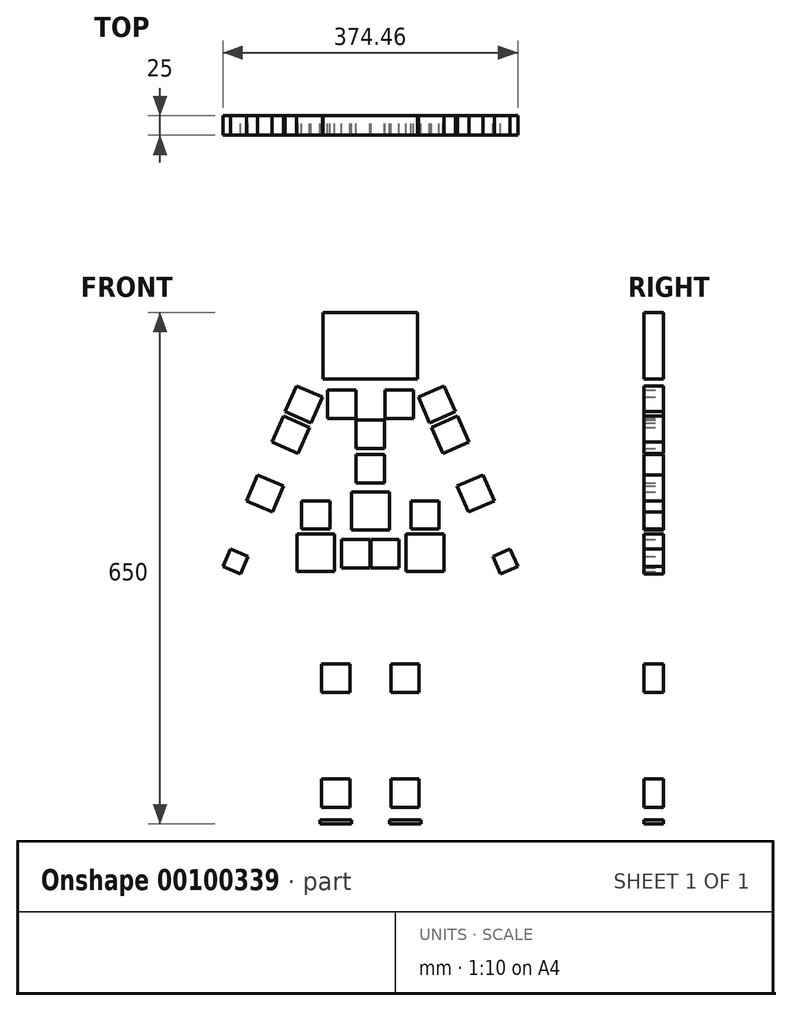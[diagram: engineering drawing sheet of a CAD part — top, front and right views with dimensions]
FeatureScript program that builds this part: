
annotation { "Feature Type Name" : "Feature", "Feature Type Description" : "" }
export const myFeature = defineFeature(function(context is Context, id is Id, definition is map)
    precondition{}
    {
        {
            var Q0;
            Q0=qCreatedBy(makeId("Front.planeOp"),FACE);
            var sketch = newSketch(context, id + "F0", { "sketchPlane" : qUnion([Q0])});
            skLineSegment(sketch, "E0.bottom", {"start": v(-190.27, 650) * mm, "end": v(190.27, 650) * mm, "construction": true});
            skLineSegment(sketch, "E0.top", {"start": v(-190.27, 0) * mm, "end": v(190.27, 0) * mm, "construction": true});
            skLineSegment(sketch, "E0.left", {"start": v(-190.27, 650) * mm, "end": v(-190.27, 0) * mm, "construction": true});
            skLineSegment(sketch, "E0.right", {"start": v(190.27, 650) * mm, "end": v(190.27, 0) * mm, "construction": true});
            skLineSegment(sketch, "E1", {"start": v(-190.27, 344.5) * mm, "end": v(190.27, 344.5) * mm, "construction": true});
            skLineSegment(sketch, "E2", {"start": v(-190.27, 234) * mm, "end": v(190.27, 234) * mm, "construction": true});
            skLineSegment(sketch, "E3", {"start": v(-190.27, 409.5) * mm, "end": v(190.27, 409.5) * mm, "construction": true});
            skLineSegment(sketch, "E4", {"start": v(-84.5, 650) * mm, "end": v(-84.5, 344.5) * mm, "construction": true});
            skLineSegment(sketch, "E5", {"start": v(84.5, 650) * mm, "end": v(84.5, 344.5) * mm, "construction": true});
            skLineSegment(sketch, "E6", {"start": v(0, 0) * mm, "end": v(0, 650) * mm, "construction": true});
            skLineSegment(sketch, "E7", {"start": v(-65, 344.5) * mm, "end": v(-65, 0) * mm, "construction": true});
            skLineSegment(sketch, "E8", {"start": v(65, 344.5) * mm, "end": v(65, 0) * mm, "construction": true});
            skLineSegment(sketch, "E9", {"start": v(-84.5, 565.5) * mm, "end": v(84.5, 565.5) * mm, "construction": true});
            skLineSegment(sketch, "E10", {"start": v(-190.27, 315.25) * mm, "end": v(190.27, 315.25) * mm, "construction": true});
            skLineSegment(sketch, "E11", {"start": v(-84.5, 471.25) * mm, "end": v(84.5, 471.25) * mm, "construction": true});
            skLineSegment(sketch, "E12", {"start": v(-65, 185.25) * mm, "end": v(65, 185.25) * mm, "construction": true});
            skLineSegment(sketch, "E13", {"start": v(-65, 39) * mm, "end": v(65, 39) * mm, "construction": true});
            skLineSegment(sketch, "E14", {"start": v(-84.5, 533) * mm, "end": v(84.5, 533) * mm, "construction": true});
            skSolve(sketch);
        }
        {
            var Q0;
            Q0=qCreatedBy(makeId("Front.planeOp"),FACE);
            var sketch = newSketch(context, id + "F1", { "sketchPlane" : qUnion([Q0])});
            skLineSegment(sketch, "E15", {"start": v(0, 344.5) * mm, "end": v(69.4, 344.5) * mm, "construction": true});
            skLineSegment(sketch, "E16", {"start": v(69.4, 344.5) * mm, "end": v(44, 185.25) * mm, "construction": true});
            skLineSegment(sketch, "E17", {"start": v(44, 185.25) * mm, "end": v(44, 39) * mm, "construction": true});
            skLineSegment(sketch, "E18", {"start": v(44, 39) * mm, "end": v(44, 0) * mm, "construction": true});
            skLineSegment(sketch, "E19", {"start": v(0, 0) * mm, "end": v(0, 650) * mm, "construction": true});
            skLineSegment(sketch, "E20.bottom", {"start": v(62, 21) * mm, "end": v(26, 21) * mm});
            skLineSegment(sketch, "E20.top", {"start": v(62, 57) * mm, "end": v(26, 57) * mm});
            skLineSegment(sketch, "E20.left", {"start": v(62, 21) * mm, "end": v(62, 57) * mm});
            skLineSegment(sketch, "E20.right", {"start": v(26, 21) * mm, "end": v(26, 57) * mm});
            skPoint(sketch, "E20.middle", {"position": v(44, 39) * mm});
            skLineSegment(sketch, "E21.bottom", {"start": v(62, 167.25) * mm, "end": v(26, 167.25) * mm});
            skLineSegment(sketch, "E21.top", {"start": v(62, 203.25) * mm, "end": v(26, 203.25) * mm});
            skLineSegment(sketch, "E21.left", {"start": v(62, 167.25) * mm, "end": v(62, 203.25) * mm});
            skLineSegment(sketch, "E21.right", {"start": v(26, 167.25) * mm, "end": v(26, 203.25) * mm});
            skPoint(sketch, "E21.middle", {"position": v(44, 185.25) * mm});
            skLineSegment(sketch, "E22.bottom", {"start": v(93.4, 320.5) * mm, "end": v(45.4, 320.5) * mm});
            skLineSegment(sketch, "E22.top", {"start": v(93.4, 368.5) * mm, "end": v(45.4, 368.5) * mm});
            skLineSegment(sketch, "E22.left", {"start": v(93.4, 320.5) * mm, "end": v(93.4, 368.5) * mm});
            skLineSegment(sketch, "E22.right", {"start": v(45.4, 320.5) * mm, "end": v(45.4, 368.5) * mm});
            skPoint(sketch, "E22.middle", {"position": v(69.4, 344.5) * mm});
            skLineSegment(sketch, "E23.bottom", {"start": v(87.4, 374.5) * mm, "end": v(51.4, 374.5) * mm});
            skLineSegment(sketch, "E23.top", {"start": v(87.4, 410.5) * mm, "end": v(51.4, 410.5) * mm});
            skLineSegment(sketch, "E23.left", {"start": v(87.4, 374.5) * mm, "end": v(87.4, 410.5) * mm});
            skLineSegment(sketch, "E23.right", {"start": v(51.4, 374.5) * mm, "end": v(51.4, 410.5) * mm});
            skPoint(sketch, "E23.middle", {"position": v(69.4, 392.5) * mm});
            skLineSegment(sketch, "E24.bottom", {"start": v(36.5, 325.5) * mm, "end": v(0.5, 325.5) * mm});
            skLineSegment(sketch, "E24.top", {"start": v(36.5, 361.5) * mm, "end": v(0.5, 361.5) * mm});
            skLineSegment(sketch, "E24.left", {"start": v(36.5, 325.5) * mm, "end": v(36.5, 361.5) * mm});
            skLineSegment(sketch, "E24.right", {"start": v(0.5, 325.5) * mm, "end": v(0.5, 361.5) * mm});
            skPoint(sketch, "E24.middle", {"position": v(18.5, 343.5) * mm});
            skLineSegment(sketch, "E25.bottom", {"start": v(24, 373.5) * mm, "end": v(-24, 373.5) * mm});
            skLineSegment(sketch, "E25.top", {"start": v(24, 421.5) * mm, "end": v(-24, 421.5) * mm});
            skLineSegment(sketch, "E25.left", {"start": v(24, 373.5) * mm, "end": v(24, 421.5) * mm});
            skLineSegment(sketch, "E25.right", {"start": v(-24, 373.5) * mm, "end": v(-24, 421.5) * mm});
            skPoint(sketch, "E25.middle", {"position": v(0, 397.5) * mm});
            skLineSegment(sketch, "E26.bottom", {"start": v(18, 433.5) * mm, "end": v(-18, 433.5) * mm});
            skLineSegment(sketch, "E26.top", {"start": v(18, 469.5) * mm, "end": v(-18, 469.5) * mm});
            skLineSegment(sketch, "E26.left", {"start": v(18, 433.5) * mm, "end": v(18, 469.5) * mm});
            skLineSegment(sketch, "E26.right", {"start": v(-18, 433.5) * mm, "end": v(-18, 469.5) * mm});
            skPoint(sketch, "E26.middle", {"position": v(0, 451.5) * mm});
            skLineSegment(sketch, "E27.bottom", {"start": v(18, 477.25) * mm, "end": v(-18, 477.25) * mm});
            skLineSegment(sketch, "E27.top", {"start": v(18, 513.25) * mm, "end": v(-18, 513.25) * mm});
            skLineSegment(sketch, "E27.left", {"start": v(18, 477.25) * mm, "end": v(18, 513.25) * mm});
            skLineSegment(sketch, "E27.right", {"start": v(-18, 477.25) * mm, "end": v(-18, 513.25) * mm});
            skPoint(sketch, "E27.middle", {"position": v(0, 495.25) * mm});
            skLineSegment(sketch, "E28.MirrorCS", {"start": v(-26, 21) * mm, "end": v(-26, 57) * mm});
            skLineSegment(sketch, "E29.MirrorCS", {"start": v(-51.4, 374.5) * mm, "end": v(-51.4, 410.5) * mm});
            skLineSegment(sketch, "E30.MirrorCS", {"start": v(-87.4, 374.5) * mm, "end": v(-87.4, 410.5) * mm});
            skPoint(sketch, "E31.MirrorP", {"position": v(-44, 39) * mm});
            skLineSegment(sketch, "E32.MirrorCS", {"start": v(-93.4, 320.5) * mm, "end": v(-45.4, 320.5) * mm});
            skLineSegment(sketch, "E33.MirrorCS", {"start": v(-93.4, 368.5) * mm, "end": v(-45.4, 368.5) * mm});
            skLineSegment(sketch, "E34.MirrorCS", {"start": v(-87.4, 410.5) * mm, "end": v(-51.4, 410.5) * mm});
            skLineSegment(sketch, "E35.MirrorCS", {"start": v(-36.5, 361.5) * mm, "end": v(-0.5, 361.5) * mm});
            skLineSegment(sketch, "E36.MirrorCS", {"start": v(-62, 21) * mm, "end": v(-62, 57) * mm});
            skLineSegment(sketch, "E37.MirrorCS", {"start": v(-62, 57) * mm, "end": v(-26, 57) * mm});
            skLineSegment(sketch, "E38.MirrorCS", {"start": v(-62, 167.25) * mm, "end": v(-26, 167.25) * mm});
            skLineSegment(sketch, "E39.MirrorCS", {"start": v(-93.4, 320.5) * mm, "end": v(-93.4, 368.5) * mm});
            skLineSegment(sketch, "E40.MirrorCS", {"start": v(-62, 203.25) * mm, "end": v(-26, 203.25) * mm});
            skLineSegment(sketch, "E41.MirrorCS", {"start": v(0, 344.5) * mm, "end": v(-69.4, 344.5) * mm, "construction": true});
            skLineSegment(sketch, "E42.MirrorCS", {"start": v(-62, 167.25) * mm, "end": v(-62, 203.25) * mm});
            skLineSegment(sketch, "E43.MirrorCS", {"start": v(-62, 21) * mm, "end": v(-26, 21) * mm});
            skLineSegment(sketch, "E44.MirrorCS", {"start": v(-44, 39) * mm, "end": v(-44, 0) * mm, "construction": true});
            skPoint(sketch, "E45.MirrorP", {"position": v(-69.4, 392.5) * mm});
            skLineSegment(sketch, "E46.MirrorCS", {"start": v(-87.4, 374.5) * mm, "end": v(-51.4, 374.5) * mm});
            skLineSegment(sketch, "E47.MirrorCS", {"start": v(-69.4, 344.5) * mm, "end": v(-44, 185.25) * mm, "construction": true});
            skLineSegment(sketch, "E48.MirrorCS", {"start": v(-44, 185.25) * mm, "end": v(-44, 39) * mm, "construction": true});
            skPoint(sketch, "E49.MirrorP", {"position": v(-69.4, 344.5) * mm});
            skPoint(sketch, "E50.MirrorP", {"position": v(-18.5, 343.5) * mm});
            skLineSegment(sketch, "E51.MirrorCS", {"start": v(-36.5, 325.5) * mm, "end": v(-36.5, 361.5) * mm});
            skLineSegment(sketch, "E52.MirrorCS", {"start": v(-26, 167.25) * mm, "end": v(-26, 203.25) * mm});
            skLineSegment(sketch, "E53.MirrorCS", {"start": v(-0.5, 325.5) * mm, "end": v(-0.5, 361.5) * mm});
            skPoint(sketch, "E54.MirrorP", {"position": v(-44, 185.25) * mm});
            skLineSegment(sketch, "E55.MirrorCS", {"start": v(-45.4, 320.5) * mm, "end": v(-45.4, 368.5) * mm});
            skLineSegment(sketch, "E56.MirrorCS", {"start": v(-36.5, 325.5) * mm, "end": v(-0.5, 325.5) * mm});
            skLineSegment(sketch, "E57", {"start": v(0, 533) * mm, "end": v(84.5, 533) * mm, "construction": true});
            skPoint(sketch, "E58.middle", {"position": v(84.5, 533) * mm});
            skLineSegment(sketch, "E59.bottom", {"start": v(54.5, 515) * mm, "end": v(18.5, 515) * mm});
            skLineSegment(sketch, "E59.top", {"start": v(54.5, 551) * mm, "end": v(18.5, 551) * mm});
            skLineSegment(sketch, "E59.left", {"start": v(54.5, 515) * mm, "end": v(54.5, 551) * mm});
            skLineSegment(sketch, "E59.right", {"start": v(18.5, 515) * mm, "end": v(18.5, 551) * mm});
            skPoint(sketch, "E59.middle", {"position": v(36.5, 533) * mm});
            skLineSegment(sketch, "E60", {"start": v(84.5, 533) * mm, "end": v(133.8, 419.77) * mm, "construction": true});
            skLineSegment(sketch, "E61", {"start": v(133.8, 419.77) * mm, "end": v(171.43, 333.36) * mm, "construction": true});
            skLineSegment(sketch, "E62", {"start": v(171.43, 333.36) * mm, "end": v(203.87, 258.86) * mm, "construction": true});
            skLineSegment(sketch, "E63.bottom", {"start": v(157.5, 410.45) * mm, "end": v(124.49, 396.08) * mm});
            skLineSegment(sketch, "E63.top", {"start": v(143.12, 443.46) * mm, "end": v(110.12, 429.09) * mm});
            skLineSegment(sketch, "E63.left", {"start": v(157.5, 410.45) * mm, "end": v(143.12, 443.46) * mm});
            skLineSegment(sketch, "E63.right", {"start": v(124.49, 396.08) * mm, "end": v(110.12, 429.09) * mm});
            skPoint(sketch, "E63.middle", {"position": v(133.8, 419.77) * mm});
            skLineSegment(sketch, "E64.bottom", {"start": v(124.96, 485.18) * mm, "end": v(91.95, 470.8) * mm});
            skLineSegment(sketch, "E64.top", {"start": v(110.58, 518.18) * mm, "end": v(77.58, 503.8) * mm});
            skLineSegment(sketch, "E64.left", {"start": v(124.96, 485.18) * mm, "end": v(110.58, 518.18) * mm});
            skLineSegment(sketch, "E64.right", {"start": v(91.95, 470.8) * mm, "end": v(77.58, 503.8) * mm});
            skPoint(sketch, "E64.middle", {"position": v(101.27, 494.5) * mm});
            skLineSegment(sketch, "E65.bottom", {"start": v(108.19, 523.68) * mm, "end": v(75.18, 509.31) * mm});
            skLineSegment(sketch, "E65.top", {"start": v(93.82, 556.69) * mm, "end": v(60.81, 542.32) * mm});
            skLineSegment(sketch, "E65.left", {"start": v(108.19, 523.68) * mm, "end": v(93.82, 556.69) * mm});
            skLineSegment(sketch, "E65.right", {"start": v(75.18, 509.31) * mm, "end": v(60.81, 542.32) * mm});
            skLineSegment(sketch, "E66.bottom", {"start": v(165.22, 317.56) * mm, "end": v(155.64, 339.57) * mm});
            skLineSegment(sketch, "E66.top", {"start": v(187.23, 327.14) * mm, "end": v(177.64, 349.15) * mm});
            skLineSegment(sketch, "E66.left", {"start": v(165.22, 317.56) * mm, "end": v(187.23, 327.14) * mm});
            skLineSegment(sketch, "E66.right", {"start": v(155.64, 339.57) * mm, "end": v(177.64, 349.15) * mm});
            skPoint(sketch, "E66.middle", {"position": v(171.43, 333.36) * mm});
            skPoint(sketch, "E67.MirrorP", {"position": v(-84.5, 533) * mm});
            skPoint(sketch, "E68.MirrorP", {"position": v(-101.27, 494.5) * mm});
            skPoint(sketch, "E69.MirrorP", {"position": v(-133.8, 419.77) * mm});
            skLineSegment(sketch, "E70.MirrorCS", {"start": v(-124.96, 485.18) * mm, "end": v(-110.58, 518.18) * mm});
            skLineSegment(sketch, "E71.MirrorCS", {"start": v(-155.64, 339.57) * mm, "end": v(-177.64, 349.15) * mm});
            skLineSegment(sketch, "E72.MirrorCS", {"start": v(-108.19, 523.68) * mm, "end": v(-75.18, 509.31) * mm});
            skLineSegment(sketch, "E73.MirrorCS", {"start": v(0, 533) * mm, "end": v(-84.5, 533) * mm, "construction": true});
            skLineSegment(sketch, "E74.MirrorCS", {"start": v(-171.43, 333.36) * mm, "end": v(-203.87, 258.86) * mm, "construction": true});
            skLineSegment(sketch, "E75.MirrorCS", {"start": v(-75.18, 509.31) * mm, "end": v(-60.81, 542.32) * mm});
            skLineSegment(sketch, "E76.MirrorCS", {"start": v(-91.95, 470.8) * mm, "end": v(-77.58, 503.8) * mm});
            skLineSegment(sketch, "E77.MirrorCS", {"start": v(-93.82, 556.69) * mm, "end": v(-60.81, 542.32) * mm});
            skLineSegment(sketch, "E78.MirrorCS", {"start": v(-18.5, 515) * mm, "end": v(-18.5, 551) * mm});
            skLineSegment(sketch, "E79.MirrorCS", {"start": v(-54.5, 515) * mm, "end": v(-18.5, 515) * mm});
            skLineSegment(sketch, "E80.MirrorCS", {"start": v(-157.5, 410.45) * mm, "end": v(-124.49, 396.08) * mm});
            skPoint(sketch, "E81.MirrorP", {"position": v(-171.43, 333.36) * mm});
            skLineSegment(sketch, "E82.MirrorCS", {"start": v(-143.12, 443.46) * mm, "end": v(-110.12, 429.09) * mm});
            skLineSegment(sketch, "E83.MirrorCS", {"start": v(-54.5, 551) * mm, "end": v(-18.5, 551) * mm});
            skLineSegment(sketch, "E84.MirrorCS", {"start": v(-108.19, 523.68) * mm, "end": v(-93.82, 556.69) * mm});
            skPoint(sketch, "E85.MirrorP", {"position": v(-36.5, 533) * mm});
            skLineSegment(sketch, "E86.MirrorCS", {"start": v(-165.22, 317.56) * mm, "end": v(-155.64, 339.57) * mm});
            skLineSegment(sketch, "E87.MirrorCS", {"start": v(-165.22, 317.56) * mm, "end": v(-187.23, 327.14) * mm});
            skLineSegment(sketch, "E88.MirrorCS", {"start": v(-110.58, 518.18) * mm, "end": v(-77.58, 503.8) * mm});
            skLineSegment(sketch, "E89.MirrorCS", {"start": v(-84.5, 533) * mm, "end": v(-133.8, 419.77) * mm, "construction": true});
            skLineSegment(sketch, "E90.MirrorCS", {"start": v(-133.8, 419.77) * mm, "end": v(-171.43, 333.36) * mm, "construction": true});
            skLineSegment(sketch, "E91.MirrorCS", {"start": v(-124.49, 396.08) * mm, "end": v(-110.12, 429.09) * mm});
            skLineSegment(sketch, "E92.MirrorCS", {"start": v(-54.5, 515) * mm, "end": v(-54.5, 551) * mm});
            skLineSegment(sketch, "E93.MirrorCS", {"start": v(-157.5, 410.45) * mm, "end": v(-143.12, 443.46) * mm});
            skLineSegment(sketch, "E94.MirrorCS", {"start": v(-124.96, 485.18) * mm, "end": v(-91.95, 470.8) * mm});
            skLineSegment(sketch, "E95.MirrorCS", {"start": v(-187.23, 327.14) * mm, "end": v(-177.64, 349.15) * mm});
            skLineSegment(sketch, "E96.bottom", {"start": v(60, 650) * mm, "end": v(-60, 650) * mm});
            skLineSegment(sketch, "E96.top", {"start": v(60, 565.5) * mm, "end": v(-60, 565.5) * mm});
            skLineSegment(sketch, "E96.left", {"start": v(60, 650) * mm, "end": v(60, 565.5) * mm});
            skLineSegment(sketch, "E96.right", {"start": v(-60, 650) * mm, "end": v(-60, 565.5) * mm});
            skPoint(sketch, "E96.middle", {"position": v(0, 607.75) * mm});
            skCircle(sketch, "E97", {"center": v(18.5, 343.5) * mm, "radius": 25.46 * mm, "construction": true});
            skCircle(sketch, "E98", {"center": v(0, 397.5) * mm, "radius": 33.94 * mm, "construction": true});
            skLineSegment(sketch, "E99.bottom", {"start": v(24, 5) * mm, "end": v(64, 5) * mm});
            skLineSegment(sketch, "E99.top", {"start": v(24, 0) * mm, "end": v(64, 0) * mm});
            skLineSegment(sketch, "E99.left", {"start": v(24, 5) * mm, "end": v(24, 0) * mm});
            skLineSegment(sketch, "E99.right", {"start": v(64, 5) * mm, "end": v(64, 0) * mm});
            skLineSegment(sketch, "E100.MirrorCS", {"start": v(-24, 5) * mm, "end": v(-64, 5) * mm});
            skLineSegment(sketch, "E101.MirrorCS", {"start": v(-64, 5) * mm, "end": v(-64, 0) * mm});
            skLineSegment(sketch, "E102.MirrorCS", {"start": v(-24, 5) * mm, "end": v(-24, 0) * mm});
            skLineSegment(sketch, "E103.MirrorCS", {"start": v(-24, 0) * mm, "end": v(-64, 0) * mm});
            skCircle(sketch, "E104", {"center": v(44, 39) * mm, "radius": 25.46 * mm, "construction": true});
            skCircle(sketch, "E105", {"center": v(84.5, 533) * mm, "radius": 299 * mm, "construction": true});
            skCircle(sketch, "E106", {"center": v(84.5, 533) * mm, "radius": 123.5 * mm, "construction": true});
            skCircle(sketch, "E107", {"center": v(84.5, 533) * mm, "radius": 217.75 * mm, "construction": true});
            skSolve(sketch);
        }
        {
            var Q0;
            Q0 = qSketchRegion(id + "F1", true);
            extrude(context, id + "F2", {"entities" : qUnion([Q0]), "depth" : 25 * mm});
        }
    });
